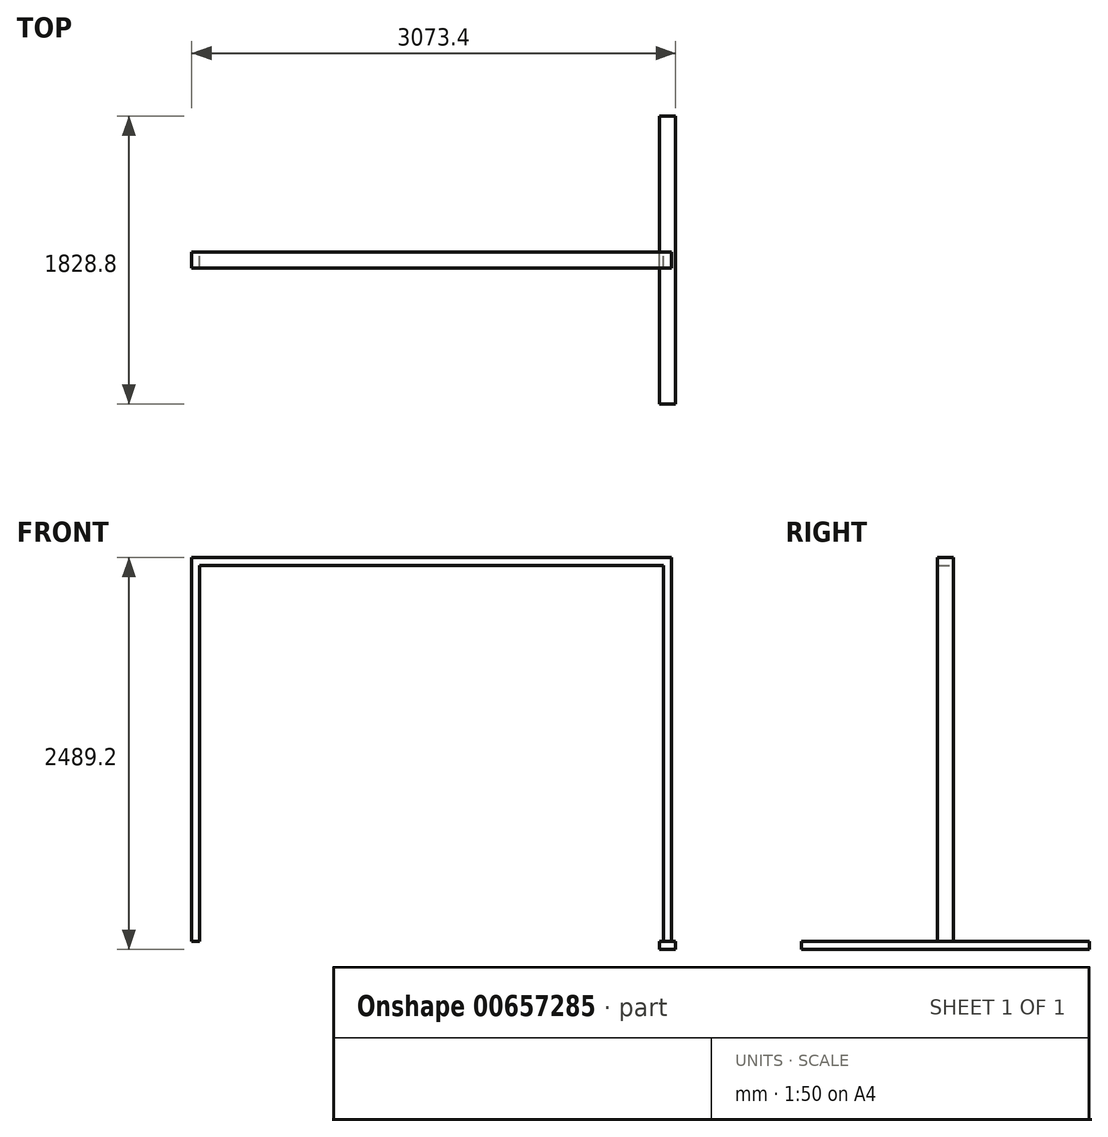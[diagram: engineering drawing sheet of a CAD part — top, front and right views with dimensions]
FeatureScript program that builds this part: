
annotation { "Feature Type Name" : "Feature", "Feature Type Description" : "" }
export const myFeature = defineFeature(function(context is Context, id is Id, definition is map)
    precondition{}
    {
        {
            var Q0;
            Q0=qCreatedBy(makeId("Front.planeOp"),FACE);
            var sketch = newSketch(context, id + "F0", { "sketchPlane" : qUnion([Q0])});
            skLineSegment(sketch, "E0", {"start": v(-49.5, 2994.94) * mm, "end": v(-49.5, 556.54) * mm});
            skLineSegment(sketch, "E1", {"start": v(-49.5, 2994.94) * mm, "end": v(2998.5, 2994.94) * mm});
            skLineSegment(sketch, "E2", {"start": v(2998.5, 2994.94) * mm, "end": v(2998.5, 556.54) * mm});
            skLineSegment(sketch, "E3.0", {"start": v(1.3, 2994.94) * mm, "end": v(1.3, 556.54) * mm});
            skLineSegment(sketch, "E4.0", {"start": v(-49.5, 2944.14) * mm, "end": v(2998.5, 2944.14) * mm});
            skLineSegment(sketch, "E5.0", {"start": v(2947.7, 2994.94) * mm, "end": v(2947.7, 556.54) * mm});
            skLineSegment(sketch, "E6", {"start": v(-49.5, 556.54) * mm, "end": v(1.3, 556.54) * mm});
            skLineSegment(sketch, "E7", {"start": v(2947.7, 556.54) * mm, "end": v(2998.5, 556.54) * mm});
            skSolve(sketch);
        }
        {
            var Q0;
            Q0 = qSketchRegion(id + "F0", true);
            extrude(context, id + "F1", {"entities" : qUnion([Q0]), "depth" : 101.6 * mm, "offsetDistance" : 25.4 * mm});
        }
        {
            var Q0;
            Q0=makeQuery(id+"F1.opExtrude","SWEPT_FACE",FACE,{"disambiguationData":[OSD([sQuery(id+"F0.wireOp",EDGE,"E2")])]});
            cPlane(context, id + "F2", {"entities" : qUnion([Q0]), "cplaneType" : CPlaneType.OFFSET, "offset" : 25.4 * mm, "width" : 152.4 * mm, "height" : 152.4 * mm});
        }
        {
            var Q0;
            Q0=qCreatedBy(id+"F2.planeOp",FACE);
            var sketch = newSketch(context, id + "F3", { "sketchPlane" : qUnion([Q0])});
            skLineSegment(sketch, "E8", {"start": v(-965.2, 556.54) * mm, "end": v(863.6, 556.54) * mm});
            skLineSegment(sketch, "E9.0", {"start": v(-965.2, 505.74) * mm, "end": v(863.6, 505.74) * mm});
            skLineSegment(sketch, "E10", {"start": v(-965.2, 556.54) * mm, "end": v(-965.2, 505.74) * mm});
            skLineSegment(sketch, "E11", {"start": v(863.6, 556.54) * mm, "end": v(863.6, 505.74) * mm});
            skSolve(sketch);
        }
        {
            var Q0;
            Q0=makeQuery(id+"F3.imprint","IMPRINT",FACE,{"disambiguationData":[TD([[makeQuery(id+"F3.imprint","IMPRINT",EDGE,{"derivedFrom":sQuery(id+"F3.wireOp",EDGE,"E8")}),-1.0]])]});
            extrude(context, id + "F4", {"entities" : qUnion([Q0]), "oppositeDirection" : true, "depth" : 101.6 * mm, "offsetDistance" : 25.4 * mm});
        }
    });
